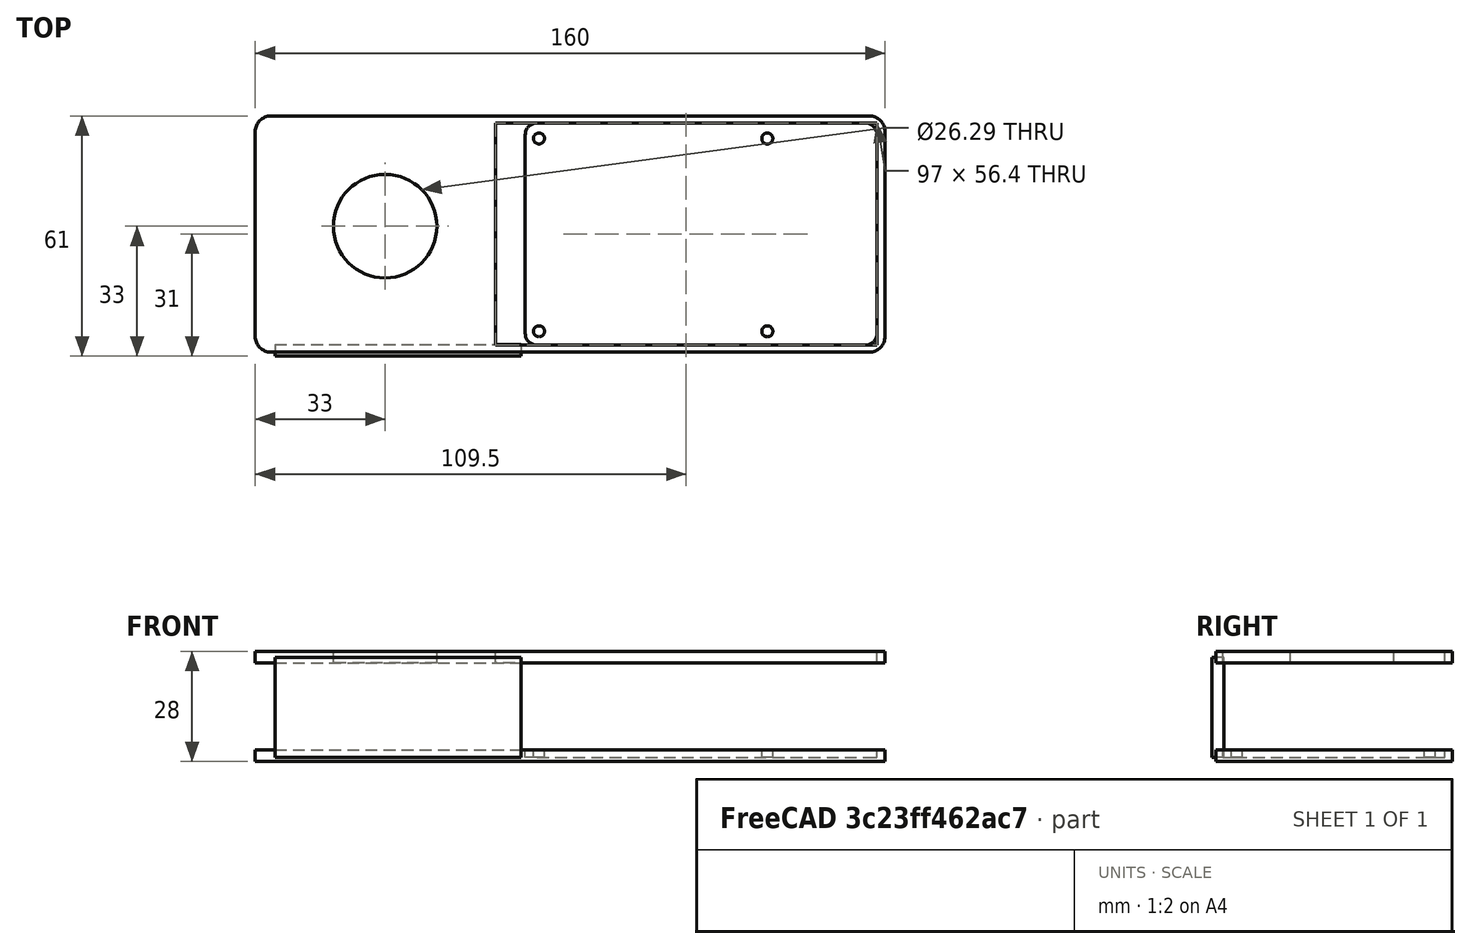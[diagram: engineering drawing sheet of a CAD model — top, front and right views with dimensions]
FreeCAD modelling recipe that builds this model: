
FCSTD DOCUMENT  (FreeCAD 0.16R)
Label: chassis
License: All rights reserved
LicenseURL: http://en.wikipedia.org/wiki/All_rights_reserved
objects: Part::Cut×3, Part::Feature×2, Part::Box×2, Part::Part2DObjectPython×1, PartDesign::Pad×1, PartDesign::Fillet×1, Part::Cylinder×1
note: 12 computed .brp shape members not serialized (recipe doc carries the construction recipe); baked Part::Feature solids carry a one-line shape summary decoded from their .brp

FEATURE [Part::Part2DObjectPython] Rectangle  # Draft 2D object (typed FeaturePython)
  ChamferSize = 0
  Columns = 1
  FilletRadius = 0
  Height = 60
  Length = 160
  MakeFace = true
  Placement = pos=(-114,-32,0) rot=(0,0,1;0rad)
  Rows = 1
FEATURE [Part::Feature] Cut_solid  label="pibase"
  Placement = pos=(-0.4,-0.2,1.1) rot=(0,0,1;0rad)
  shape: bbox 89.4 x 56.4 x 2 mm, 14 faces (baked)
FEATURE [PartDesign::Pad] Pad
  Length = 3
  Length2 = 100
  Placement = pos=(-114,-32,0) rot=(0,0,1;0rad)
  Sketch = -> Rectangle
  Type = 0
FEATURE [PartDesign::Fillet] Fillet
  Base = -> Pad [Edge5,Edge2,Edge1,Edge8]
  Placement = pos=(-114,-32,0) rot=(0,0,1;0rad)
  Radius = 4
FEATURE [Part::Cut] Cut
  Base = -> Fillet
  Tool = -> Cut_solid
FEATURE [Part::Feature] Fillet001_solid  label="Fillet001 (Solid)"
  Placement = pos=(0,0,17) rot=(0,0,1;0rad)
  shape: bbox 160 x 60 x 3 mm, 10 faces (baked)
FEATURE [Part::Box] Box  label="Cube"
  Height = 5
  Length = 97
  Placement = pos=(-53,-30.2,16) rot=(0,0,1;0rad)
  Width = 56.4
FEATURE [Part::Cut] Cut001
  Base = -> Fillet001_solid
  Tool = -> Box
FEATURE [Part::Cylinder] Cylinder  label="Cylindre"
  Angle = 360
  Height = 10
  Placement = pos=(-81,0,13) rot=(0,0,1;0rad)
  Radius = 13.1445
FEATURE [Part::Cut] Cut002
  Base = -> Cut001
  Placement = pos=(0,0,8) rot=(0,0,1;0rad)
  Tool = -> Cylinder
FEATURE [Part::Box] Box001  label="Cube001"
  Height = 3
  Length = 62.5
  Placement = pos=(-109,-30,1) rot=(1,0,0;1.5708rad)
  Width = 25.4
